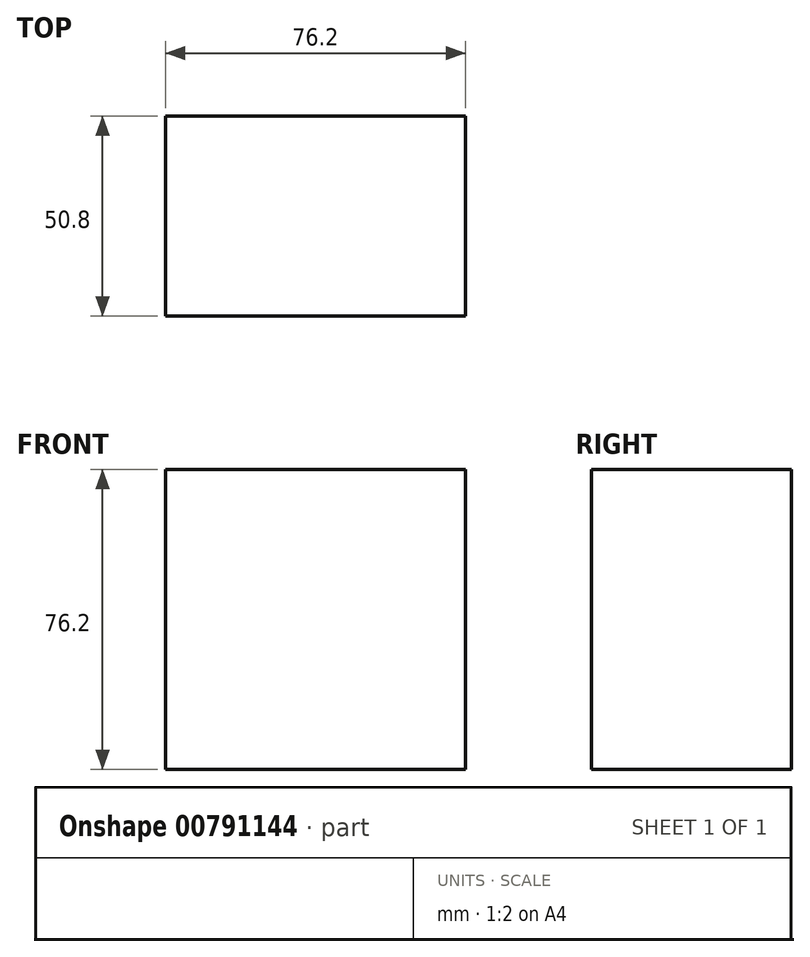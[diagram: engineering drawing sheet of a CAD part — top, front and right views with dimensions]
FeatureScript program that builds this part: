
annotation { "Feature Type Name" : "Feature", "Feature Type Description" : "" }
export const myFeature = defineFeature(function(context is Context, id is Id, definition is map)
    precondition{}
    {
        {
            var Q0;
            Q0=qCreatedBy(makeId("Front.planeOp"),FACE);
            var sketch = newSketch(context, id + "F0", { "sketchPlane" : qUnion([Q0])});
            skLineSegment(sketch, "E0.bottom", {"start": v(-38.54, 47.5) * mm, "end": v(37.66, 47.5) * mm});
            skLineSegment(sketch, "E0.top", {"start": v(-38.54, -28.7) * mm, "end": v(37.66, -28.7) * mm});
            skLineSegment(sketch, "E0.left", {"start": v(-38.54, 47.5) * mm, "end": v(-38.54, -28.7) * mm});
            skLineSegment(sketch, "E0.right", {"start": v(37.66, 47.5) * mm, "end": v(37.66, -28.7) * mm});
            skSolve(sketch);
        }
        {
            var Q0;
            Q0 = qSketchRegion(id + "F0", true);
            extrude(context, id + "F1", {"entities" : qUnion([Q0]), "depth" : -50.8 * mm, "offsetDistance" : 25.4 * mm});
        }
    });
